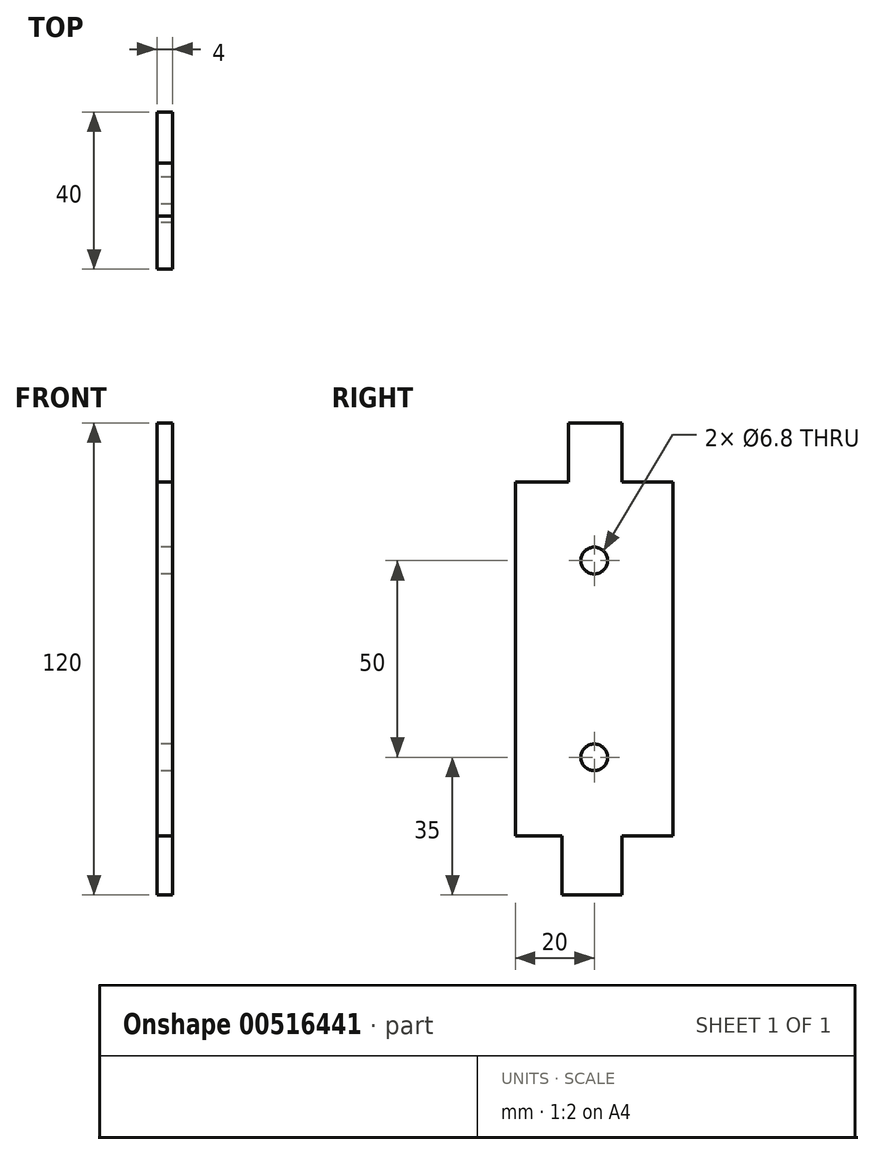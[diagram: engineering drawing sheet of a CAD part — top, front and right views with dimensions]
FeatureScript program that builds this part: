
annotation { "Feature Type Name" : "Feature", "Feature Type Description" : "" }
export const myFeature = defineFeature(function(context is Context, id is Id, definition is map)
    precondition{}
    {
        {
            var Q0;
            Q0=qCreatedBy(makeId("Right.planeOp"),FACE);
            var sketch = newSketch(context, id + "F0", { "sketchPlane" : qUnion([Q0])});
            skLineSegment(sketch, "E0.bottom", {"start": v(-8.17, -60) * mm, "end": v(7, -60) * mm});
            skLineSegment(sketch, "E0.top", {"start": v(-6.5, 60) * mm, "end": v(7, 60) * mm});
            skLineSegment(sketch, "E0.left", {"start": v(-20, -45) * mm, "end": v(-20, 45) * mm});
            skLineSegment(sketch, "E0.right", {"start": v(20, -45) * mm, "end": v(20, 45) * mm});
            skPoint(sketch, "E0.middle", {"position": v(0, 0) * mm});
            skLineSegment(sketch, "E1.top", {"start": v(-20, 45) * mm, "end": v(-6.5, 45) * mm});
            skLineSegment(sketch, "E1.right", {"start": v(-6.5, 60) * mm, "end": v(-6.5, 45) * mm});
            skLineSegment(sketch, "E2.top", {"start": v(20, 45) * mm, "end": v(7, 45) * mm});
            skLineSegment(sketch, "E2.right", {"start": v(7, 60) * mm, "end": v(7, 45) * mm});
            skLineSegment(sketch, "E3.top", {"start": v(-20, -45) * mm, "end": v(-8.17, -45) * mm});
            skLineSegment(sketch, "E3.right", {"start": v(-8.17, -60) * mm, "end": v(-8.17, -45) * mm});
            skLineSegment(sketch, "E4.top", {"start": v(20, -45) * mm, "end": v(7, -45) * mm});
            skLineSegment(sketch, "E4.right", {"start": v(7, -60) * mm, "end": v(7, -45) * mm});
            skPoint(sketch, "E5.orphan", {"position": v(20, 60) * mm});
            skPoint(sketch, "E6.orphan", {"position": v(-20, 60) * mm});
            skPoint(sketch, "E7.orphan", {"position": v(-20, -60) * mm});
            skPoint(sketch, "E8.orphan", {"position": v(20, -60) * mm});
            skCircle(sketch, "E9", {"center": v(0, 25) * mm, "radius": 3.4 * mm});
            skCircle(sketch, "E10", {"center": v(0, -25) * mm, "radius": 3.4 * mm});
            skSolve(sketch);
        }
        {
            var Q0;
            Q0 = qSketchRegion(id + "F0", true);
            extrude(context, id + "F1", {"entities" : qUnion([Q0]), "depth" : 4 * mm, "offsetDistance" : 25 * mm});
        }
    });
